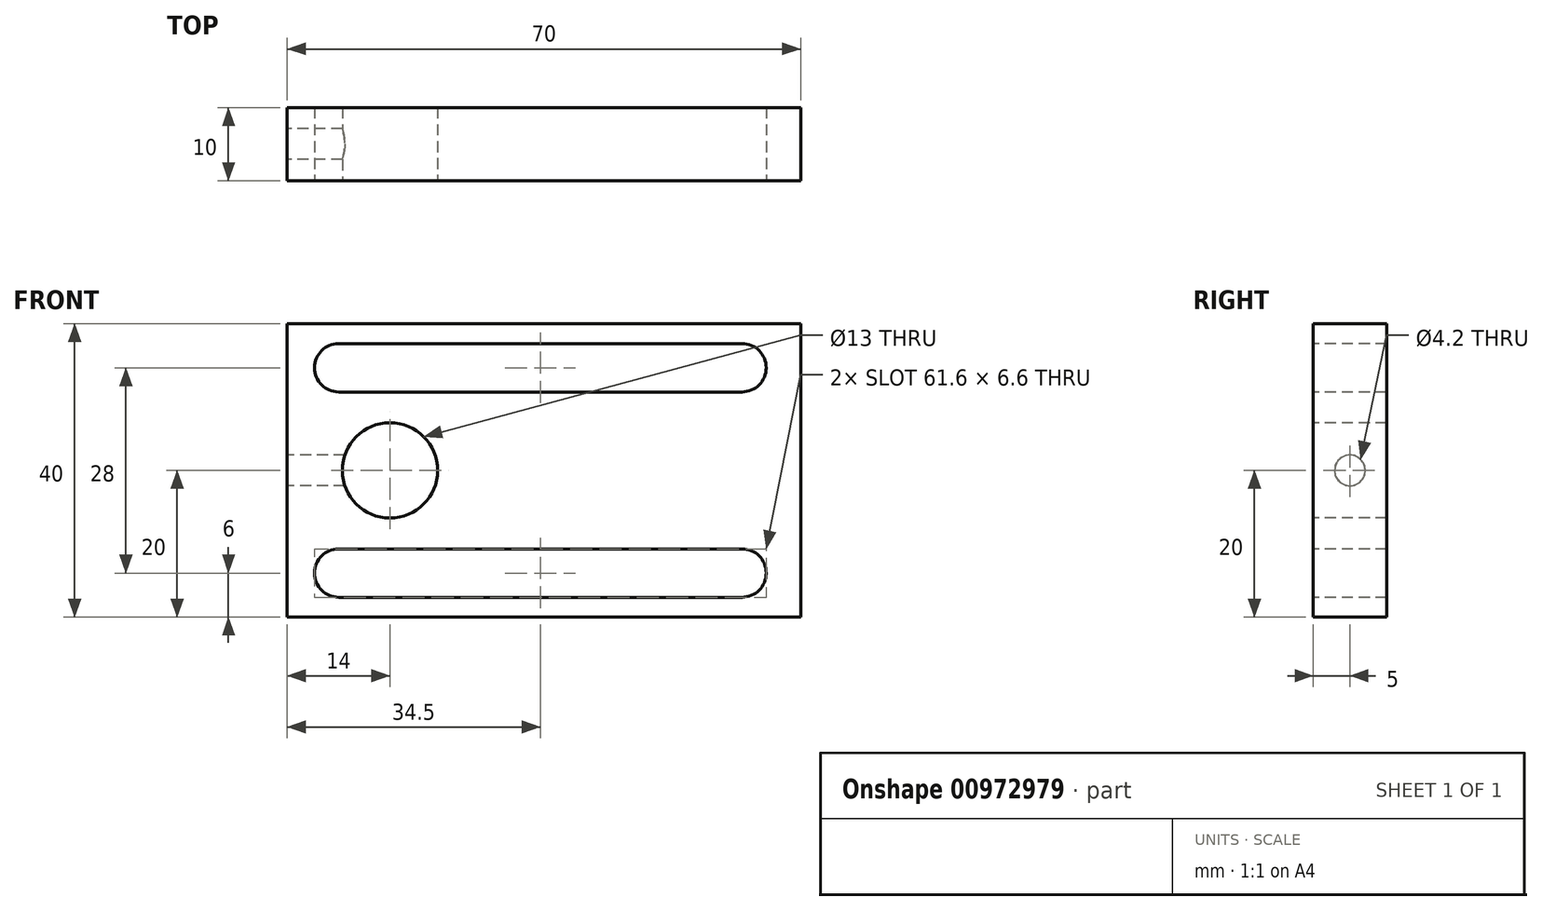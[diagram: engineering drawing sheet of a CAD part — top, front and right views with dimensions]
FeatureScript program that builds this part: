
annotation { "Feature Type Name" : "Feature", "Feature Type Description" : "" }
export const myFeature = defineFeature(function(context is Context, id is Id, definition is map)
    precondition{}
    {
        {
            var Q0;
            Q0=qCreatedBy(makeId("Front.planeOp"),FACE);
            var sketch = newSketch(context, id + "F0", { "sketchPlane" : qUnion([Q0])});
            skLineSegment(sketch, "E0.bottom", {"start": v(0, 0) * mm, "end": v(70, 0) * mm});
            skLineSegment(sketch, "E0.top", {"start": v(0, 40) * mm, "end": v(70, 40) * mm});
            skLineSegment(sketch, "E0.left", {"start": v(0, 0) * mm, "end": v(0, 40) * mm});
            skLineSegment(sketch, "E0.right", {"start": v(70, 0) * mm, "end": v(70, 40) * mm});
            skSolve(sketch);
        }
        {
            var Q0;
            Q0=makeQuery(id+"F0.imprint","IMPRINT",FACE,{"disambiguationData":[TD([[makeQuery(id+"F0.imprint","IMPRINT",EDGE,{"derivedFrom":sQuery(id+"F0.wireOp",EDGE,"E0.bottom")}),1.0]])]});
            extrude(context, id + "F1", {"entities" : qUnion([Q0]), "depth" : 10 * mm, "offsetDistance" : 25 * mm});
        }
        {
            var Q0;
            Q0=makeQuery(id+"F1.opExtrude","CAP_FACE",FACE,{"disambiguationData":[OSD([sQuery(id+"F0.wireOp",EDGE,"E0.bottom"),sQuery(id+"F0.wireOp",EDGE,"E0.top"),sQuery(id+"F0.wireOp",EDGE,"E0.left"),sQuery(id+"F0.wireOp",EDGE,"E0.right")])],"isStart":false});
            var sketch = newSketch(context, id + "F2", { "sketchPlane" : qUnion([Q0])});
            skPoint(sketch, "E1", {"position": v(62, 34) * mm});
            skPoint(sketch, "E2", {"position": v(62, 6) * mm});
            skPoint(sketch, "E3", {"position": v(7, 6) * mm});
            skPoint(sketch, "E4", {"position": v(7, 34) * mm});
            skPoint(sketch, "E5", {"position": v(14, 20) * mm});
            skPoint(sketch, "E5.positionSnap0", {"position": v(0, 20) * mm});
            skCircle(sketch, "E6", {"center": v(14, 20) * mm, "radius": 6.5 * mm});
            skCircle(sketch, "E7", {"center": v(62, 34) * mm, "radius": 3.3 * mm});
            skCircle(sketch, "E8", {"center": v(7, 34) * mm, "radius": 3.3 * mm});
            skCircle(sketch, "E9", {"center": v(7, 6) * mm, "radius": 3.3 * mm});
            skCircle(sketch, "E10", {"center": v(62, 6) * mm, "radius": 3.3 * mm});
            skLineSegment(sketch, "E11", {"start": v(7, 9.3) * mm, "end": v(62, 9.3) * mm});
            skLineSegment(sketch, "E12", {"start": v(62, 9.3) * mm, "end": v(62, 2.7) * mm});
            skLineSegment(sketch, "E13", {"start": v(62, 2.7) * mm, "end": v(7, 2.7) * mm});
            skLineSegment(sketch, "E14", {"start": v(7, 30.7) * mm, "end": v(62, 30.7) * mm});
            skLineSegment(sketch, "E15", {"start": v(62, 30.7) * mm, "end": v(62, 37.3) * mm});
            skLineSegment(sketch, "E16", {"start": v(62, 37.3) * mm, "end": v(7, 37.3) * mm});
            skSolve(sketch);
        }
        {
            var Q0;
            {var subQ0=sQuery(id+"F2.wireOp",EDGE,"E15");Q0=makeQuery(id+"F2.imprint","IMPRINT",FACE,{"disambiguationData":[TD([[makeQuery(id+"F2.imprint","IMPRINT",EDGE,{"derivedFrom":subQ0}),1.0]])]});}
            var Q1;
            {var subQ0=sQuery(id+"F2.wireOp",EDGE,"E15");Q1=makeQuery(id+"F2.imprint","IMPRINT",FACE,{"disambiguationData":[TD([[makeQuery(id+"F2.imprint","IMPRINT",EDGE,{"derivedFrom":subQ0}),-1.0]])]});}
            var Q2;
            {var subQ0=sQuery(id+"F2.wireOp",EDGE,"E8");var subQ1=makeQuery(id+"F2.imprint","INTERSECT",VERTEX,{"derivedFrom":[subQ0,sQuery(id+"F2.wireOp",EDGE,"E14")]});Q2=makeQuery(id+"F2.imprint","IMPRINT",FACE,{"disambiguationData":[TD([[makeQuery(id+"F2.imprint","IMPRINT",EDGE,{"disambiguationData":[TD([[subQ1,1.0]])],"derivedFrom":subQ0}),1.0]])]});}
            var Q3;
            {var subQ0=sQuery(id+"F2.wireOp",EDGE,"E9");var subQ1=makeQuery(id+"F2.imprint","INTERSECT",VERTEX,{"derivedFrom":[subQ0,sQuery(id+"F2.wireOp",EDGE,"E11")]});Q3=makeQuery(id+"F2.imprint","IMPRINT",FACE,{"disambiguationData":[TD([[makeQuery(id+"F2.imprint","IMPRINT",EDGE,{"disambiguationData":[TD([[subQ1,-1.0]])],"derivedFrom":subQ0}),1.0]])]});}
            var Q4;
            {var subQ0=sQuery(id+"F2.wireOp",EDGE,"E12");Q4=makeQuery(id+"F2.imprint","IMPRINT",FACE,{"disambiguationData":[TD([[makeQuery(id+"F2.imprint","IMPRINT",EDGE,{"derivedFrom":subQ0}),-1.0]])]});}
            var Q5;
            {var subQ0=sQuery(id+"F2.wireOp",EDGE,"E12");Q5=makeQuery(id+"F2.imprint","IMPRINT",FACE,{"disambiguationData":[TD([[makeQuery(id+"F2.imprint","IMPRINT",EDGE,{"derivedFrom":subQ0}),1.0]])]});}
            var Q6;
            {var subQ1=sQuery(id+"F2.wireOp",EDGE,"E14");Q6=makeQuery(id+"F2.imprint","IMPRINT",FACE,{"disambiguationData":[TD([[makeQuery(id+"F2.imprint","IMPRINT",EDGE,{"derivedFrom":subQ1}),1.0]])]});}
            var Q7;
            {var subQ0=sQuery(id+"F2.wireOp",EDGE,"E11");Q7=makeQuery(id+"F2.imprint","IMPRINT",FACE,{"disambiguationData":[TD([[makeQuery(id+"F2.imprint","IMPRINT",EDGE,{"derivedFrom":subQ0}),-1.0]])]});}
            var Q8;
            Q8=makeQuery(id+"F2.imprint","IMPRINT",FACE,{"disambiguationData":[TD([[makeQuery(id+"F2.imprint","IMPRINT",EDGE,{"derivedFrom":sQuery(id+"F2.wireOp",EDGE,"E6")}),1.0]])]});
            extrude(context, id + "F3", {"entities" : qUnion([Q0, Q1, Q2, Q3, Q4, Q5, Q6, Q7, Q8]), "operationType" : NewBodyOperationType.REMOVE, "oppositeDirection" : true, "depth" : 25 * mm, "offsetDistance" : 25 * mm});
        }
        {
            var Q0;
            Q0=makeQuery(id+"F1.opExtrude","SWEPT_FACE",FACE,{"disambiguationData":[OSD([sQuery(id+"F0.wireOp",EDGE,"E0.left")])]});
            var sketch = newSketch(context, id + "F4", { "sketchPlane" : qUnion([Q0])});
            skPoint(sketch, "E17", {"position": v(5, 20) * mm});
            skPoint(sketch, "E17.positionSnap0", {"position": v(10, 20) * mm});
            skPoint(sketch, "E17.positionSnap1", {"position": v(5, 40) * mm});
            skSolve(sketch);
        }
        {
            var Q0;
            Q0=sQuery(id+"F4.wireOp",VERTEX,"E17");
            var Q1;
            Q1=makeQuery(id+"F1.opExtrude","SWEPT_BODY",BODY,{"disambiguationData":[OSD([sQuery(id+"F0.wireOp",EDGE,"E0.bottom"),sQuery(id+"F0.wireOp",EDGE,"E0.top"),sQuery(id+"F0.wireOp",EDGE,"E0.left"),sQuery(id+"F0.wireOp",EDGE,"E0.right")])]});
            hole(context, id + "F5", {"style" : HoleStyle.SIMPLE, "endStyle" : HoleEndStyle.BLIND, "standardTappedOrClearance" : lookupTablePath({ "standard" : "ISO", "engagement" : "75%", "pitch" : "0.8 mm", "size" : "M5", "type" : "Tapped" }), "standardBlindInLast" : lookupTablePath({ "standard" : "ISO", "fit" : "Normal", "engagement" : "75%", "pitch" : "0.8 mm", "size" : "M5", "type" : "Clearance & tapped" }), "holeDiameter" : 4.2 * mm, "majorDiameter" : 5 * mm, "showTappedDepth" : true, "holeDepth" : 15 * mm, "isTappedThrough" : true, "tappedDepth" : 12.6 * mm, "tapClearance" : 3, "startFromSketch" : true, "locations" : qUnion([Q0]), "scope" : qUnion([Q1])});
        }
    });
